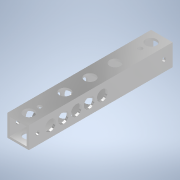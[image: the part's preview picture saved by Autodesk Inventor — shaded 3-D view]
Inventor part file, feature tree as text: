
AUTODESK INVENTOR PART (.ipt)
format: ipt  version: 2020.3 (Build 243373000, 373)  size: 201,728 bytes
history: native  units: mm
features: sketch x5, hole x4, other x1, extrude x1
ambient origin geometry x8: Origin, YZ Plane, XZ Plane, XY Plane, X Axis, Y Axis, Z Axis, Center Point
bodies: Body1 (feature_tree)
feature tree (11):
  other  "ソリッド1"
  extrude  "押し出し1"  Depth=15.0mm
  hole  "穴1"  [1 undecoded]
  hole  "穴2"  [1 undecoded]
  hole  "穴3"  [1 undecoded]
  hole  "穴4"  [1 undecoded]
  sketch  "スケッチ1"
  sketch  "スケッチ2"
  sketch  "スケッチ3"
  sketch  "スケッチ4"
  sketch  "スケッチ5"
note: 4 required parameter values undecoded (feature->parameter linkage not recoverable at this tier; creation-order binding heuristic only, values carry confidence <= 0.55)
